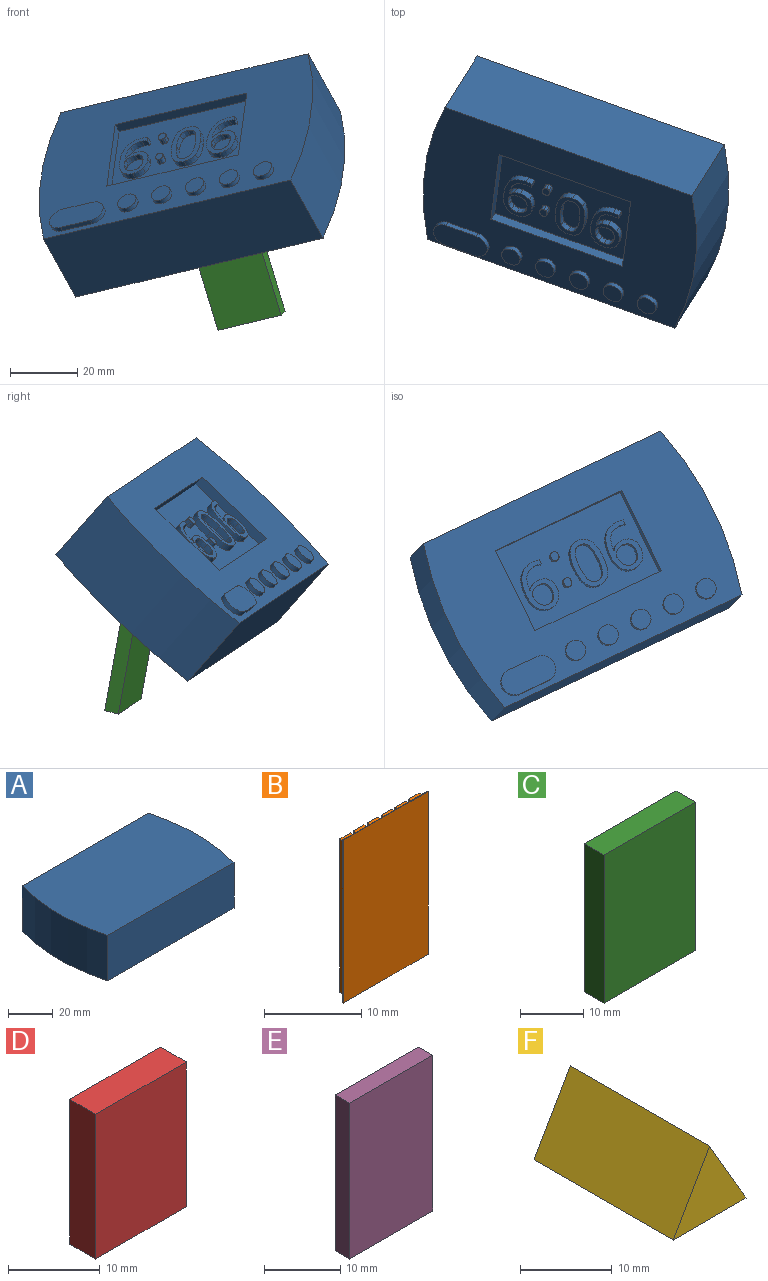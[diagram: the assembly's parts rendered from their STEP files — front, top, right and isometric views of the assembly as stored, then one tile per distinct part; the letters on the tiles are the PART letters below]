
ASSEMBLY  parts=6 mates=5
PART A: 116 faces, bbox 87.7x54.6x26.5 mm
  f0: plane 87.67x54.61mm, normal (0,0,-1), area 3248.2mm2, adj f1,f2,f3,f4,f6,f7,f8,f9
  f1: cylinder r=101.04mm len=54.61mm, axis (0,0,-1), area 1382.4mm2, adj f0,f2,f4,f5
  f2: plane 80.15x25mm, normal (0,-1,0), area 2003.7mm2, adj f0,f1,f3,f5
  f3: cylinder r=101.04mm len=54.61mm, axis (0,0,-1), area 1382.4mm2, adj f0,f2,f4,f5
  f4: plane 80.15x25mm, normal (0,1,0), area 2003.7mm2, adj f0,f1,f3,f5
  f5: plane 87.67x54.61mm, normal (0,0,1), area 4651.5mm2, adj f1,f2,f3,f4
  f6: plane 26.67x3mm, normal (1,0,0), area 80mm2, adj f0,f7,f9,f10
  f7: plane 42.67x3mm, normal (0,1,0), area 128mm2, adj f0,f6,f8,f10
  f8: plane 26.67x3mm, normal (-1,0,0), area 80mm2, adj f0,f7,f9,f10
  f9: plane 42.67x3mm, normal (0,-1,0), area 128mm2, adj f0,f6,f8,f10
  f10: plane 42.67x26.67mm, normal (0,0,-1), area 841.4mm2, adj f6,f7,f8,f9,f26,f27,f28,f29
  f11: cylinder r=3mm len=6mm, axis (0,0,1), area 28.3mm2, adj f0,f12
  f12: plane 6x6mm, normal (0,0,-1), area 28.3mm2, adj f11
  f13: cylinder r=3mm len=6mm, axis (0,0,1), area 28.3mm2, adj f0,f14
  f14: plane 6x6mm, normal (0,0,-1), area 28.3mm2, adj f13
  f15: cylinder r=3mm len=6mm, axis (0,0,1), area 28.3mm2, adj f0,f16
  f16: plane 6x6mm, normal (0,0,-1), area 28.3mm2, adj f15
  f17: cylinder r=3mm len=6mm, axis (0,0,1), area 28.3mm2, adj f0,f18
  f18: plane 6x6mm, normal (0,0,-1), area 28.3mm2, adj f17
  f19: cylinder r=3mm len=6mm, axis (0,0,1), area 28.3mm2, adj f0,f20
  f20: plane 6x6mm, normal (0,0,-1), area 28.3mm2, adj f19
  f21: plane 9.89x1.5mm, normal (-0.01,1,0), area 14.8mm2, adj f0,f22,f24,f25
  f22: cylinder r=3.92mm len=7.85mm, axis (0,0,1), area 18.5mm2, adj f0,f21,f23,f25
  f23: plane 9.46x1.5mm, normal (0,-1,0), area 14.2mm2, adj f0,f22,f24,f25
  f24: cylinder r=3.99mm len=7.95mm, axis (0,0,1), area 18.1mm2, adj f0,f21,f23,f25
  f25: plane 17.37x7.95mm, normal (0,0,-1), area 123.9mm2, adj f21,f22,f23,f24
  f26: extruded ~3.39x2mm, area 6.9mm2, adj f10,f27,f51,f52
  f27: extruded ~2.18x2mm, area 5.6mm2, adj f10,f26,f28,f52
  f28: extruded ~2.56x2mm, area 5.4mm2, adj f10,f27,f29,f52
  f29: extruded ~3.29x2mm, area 7.3mm2, adj f10,f28,f30,f52
  f30: extruded ~3.53x2mm, area 7.7mm2, adj f10,f29,f31,f52
  f31: extruded ~3.18x2mm, area 6.9mm2, adj f10,f30,f32,f52
  f32: extruded ~3.02x2mm, area 6.6mm2, adj f10,f31,f33,f52
  f33: extruded ~2.01x2mm, area 4.1mm2, adj f10,f32,f34,f52
  f34: extruded ~2x1.43mm, area 3.8mm2, adj f10,f33,f35,f52
  f35: plane 2x0.12mm, normal (0,1,0), area 0.2mm2, adj f10,f34,f36,f52
  f36: extruded ~4.46x2mm, area 9.5mm2, adj f10,f35,f37,f52
  f37: extruded ~3.55x2mm, area 8mm2, adj f10,f36,f38,f52
  f38: extruded ~2x1.78mm, area 3.6mm2, adj f10,f37,f39,f52
  f39: plane 2x1.4mm, normal (-1,0,0), area 2.8mm2, adj f10,f38,f40,f52
  f40: extruded ~2x1.8mm, area 3.6mm2, adj f10,f39,f51,f52
  f41: extruded ~2x1.65mm, area 3.5mm2, adj f42,f50,f52,f53
  f42: extruded ~2x1.37mm, area 3.6mm2, adj f41,f43,f52,f53
  f43: extruded ~2x1.9mm, area 3.9mm2, adj f42,f44,f52,f53
  f44: extruded ~2x1.31mm, area 2.8mm2, adj f43,f45,f52,f53
  f45: extruded ~2x1.18mm, area 3.1mm2, adj f44,f46,f52,f53
  f46: extruded ~2x1.64mm, area 3.4mm2, adj f45,f47,f52,f53
  f47: extruded ~2.15x2mm, area 4.7mm2, adj f46,f48,f52,f53
  f48: extruded ~2.22x2mm, area 4.8mm2, adj f47,f49,f52,f53
  f49: extruded ~2.51x2mm, area 5.4mm2, adj f48,f50,f52,f53
  f50: extruded ~2.17x2mm, area 4.9mm2, adj f41,f49,f52,f53
  f51: extruded ~8.41x6.51mm, area 24.3mm2, adj f10,f26,f40,f52
  f52: plane 14.73x9.36mm, normal (0,0,-1), area 53.2mm2, adj f26,f27,f28,f29,f30,f31,f32,f33
  f53: plane 6.44x6.11mm, normal (0,0,-1), area 31.7mm2, adj f41,f42,f43,f44,f45,f46,f47,f48
  f54: extruded ~5.48x2mm, area 11.4mm2, adj f10,f55,f69,f70
  f55: extruded ~3.54x2mm, area 8.4mm2, adj f10,f54,f56,f70
  f56: extruded ~3.56x2mm, area 8.4mm2, adj f10,f55,f57,f70
  f57: extruded ~5.56x2mm, area 11.5mm2, adj f10,f56,f58,f70
  f58: extruded ~5.51x2mm, area 11.4mm2, adj f10,f57,f59,f70
  f59: extruded ~3.52x2mm, area 8.4mm2, adj f10,f58,f60,f70
  f60: extruded ~3.58x2mm, area 8.4mm2, adj f10,f59,f69,f70
  f61: extruded ~4.54x2mm, area 9.3mm2, adj f62,f68,f70,f71
  f62: extruded ~2.34x2mm, area 5.8mm2, adj f61,f63,f70,f71
  f63: extruded ~2.36x2mm, area 5.9mm2, adj f62,f64,f70,f71
  f64: extruded ~4.52x2mm, area 9.2mm2, adj f63,f65,f70,f71
  f65: extruded ~4.54x2mm, area 9.3mm2, adj f64,f66,f70,f71
  f66: extruded ~2.36x2mm, area 5.9mm2, adj f65,f67,f70,f71
  f67: extruded ~2.34x2mm, area 5.8mm2, adj f66,f68,f70,f71
  f68: extruded ~4.55x2mm, area 9.3mm2, adj f61,f67,f70,f71
  f69: extruded ~5.55x2mm, area 11.5mm2, adj f10,f54,f60,f70
  f70: plane 14.76x9.48mm, normal (0,0,-1), area 54.2mm2, adj f54,f55,f56,f57,f58,f59,f60,f61
  f71: plane 11.94x6.16mm, normal (0,0,-1), area 62.2mm2, adj f61,f62,f63,f64,f65,f66,f67,f68
  f72: extruded ~2x1.01mm, area 2.2mm2, adj f10,f73,f79,f80
  f73: extruded ~2x0.83mm, area 1.8mm2, adj f10,f72,f74,f80
  f74: extruded ~2x0.88mm, area 1.9mm2, adj f10,f73,f75,f80
  f75: extruded ~2x0.98mm, area 2.1mm2, adj f10,f74,f76,f80
  f76: extruded ~2x1mm, area 2.1mm2, adj f10,f75,f77,f80
  f77: extruded ~2x0.89mm, area 2mm2, adj f10,f76,f78,f80
  f78: extruded ~2x0.86mm, area 1.9mm2, adj f10,f77,f79,f80
  f79: extruded ~2x1mm, area 2.1mm2, adj f10,f72,f78,f80
  f80: plane 2.66x2.36mm, normal (0,0,-1), area 5.2mm2, adj f72,f73,f74,f75,f76,f77,f78,f79
  f81: extruded ~2x1.01mm, area 2.2mm2, adj f10,f82,f86,f87
  f82: extruded ~2x0.83mm, area 1.8mm2, adj f10,f81,f83,f87
  f83: extruded ~2x0.88mm, area 1.9mm2, adj f10,f82,f84,f87
  f84: extruded ~2x0.98mm, area 2.1mm2, adj f10,f83,f85,f87
  f85: extruded ~2x1.32mm, area 4.1mm2, adj f10,f84,f86,f87
  f86: extruded ~2x1.32mm, area 4mm2, adj f10,f81,f85,f87
  f87: plane 2.65x2.36mm, normal (0,0,-1), area 5.2mm2, adj f81,f82,f83,f84,f85,f86
  f88: extruded ~3.39x2mm, area 6.9mm2, adj f10,f89,f113,f114
  f89: extruded ~2.18x2mm, area 5.6mm2, adj f10,f88,f90,f114
  f90: extruded ~2.56x2mm, area 5.4mm2, adj f10,f89,f91,f114
  f91: extruded ~3.29x2mm, area 7.3mm2, adj f10,f90,f92,f114
  f92: extruded ~3.53x2mm, area 7.7mm2, adj f10,f91,f93,f114
  f93: extruded ~3.18x2mm, area 6.9mm2, adj f10,f92,f94,f114
  f94: extruded ~3.02x2mm, area 6.6mm2, adj f10,f93,f95,f114
  f95: extruded ~2.01x2mm, area 4.1mm2, adj f10,f94,f96,f114
  f96: extruded ~2x1.43mm, area 3.8mm2, adj f10,f95,f97,f114
  f97: plane 2x0.12mm, normal (0,1,0), area 0.2mm2, adj f10,f96,f98,f114
  f98: extruded ~4.46x2mm, area 9.5mm2, adj f10,f97,f99,f114
  f99: extruded ~3.55x2mm, area 8mm2, adj f10,f98,f100,f114
  f100: extruded ~2x1.78mm, area 3.6mm2, adj f10,f99,f101,f114
  f101: plane 2x1.4mm, normal (-1,0,0), area 2.8mm2, adj f10,f100,f102,f114
  f102: extruded ~2x1.8mm, area 3.6mm2, adj f10,f101,f113,f114
  f103: extruded ~2x1.65mm, area 3.5mm2, adj f104,f112,f114,f115
  f104: extruded ~2x1.37mm, area 3.6mm2, adj f103,f105,f114,f115
  f105: extruded ~2x1.9mm, area 3.9mm2, adj f104,f106,f114,f115
  f106: extruded ~2x1.31mm, area 2.8mm2, adj f105,f107,f114,f115
  f107: extruded ~2x1.18mm, area 3.1mm2, adj f106,f108,f114,f115
  f108: extruded ~2x1.64mm, area 3.4mm2, adj f107,f109,f114,f115
  f109: extruded ~2.15x2mm, area 4.7mm2, adj f108,f110,f114,f115
  f110: extruded ~2.22x2mm, area 4.8mm2, adj f109,f111,f114,f115
  f111: extruded ~2.51x2mm, area 5.4mm2, adj f110,f112,f114,f115
  f112: extruded ~2.17x2mm, area 4.9mm2, adj f103,f111,f114,f115
  f113: extruded ~8.41x6.51mm, area 24.3mm2, adj f10,f88,f102,f114
  f114: plane 14.73x9.36mm, normal (0,0,-1), area 53.2mm2, adj f88,f89,f90,f91,f92,f93,f94,f95
  f115: plane 6.44x6.11mm, normal (0,0,-1), area 31.7mm2, adj f103,f104,f105,f106,f107,f108,f109,f110
PART B: 36 faces, bbox 12.3x1x20.5 mm
  f0: plane 19.27x0.9mm, normal (-1,0,0), area 17.3mm2, adj f1,f3,f4,f5
  f1: plane 1.5x0.9mm, normal (0,0,-1), area 1.3mm2, adj f0,f2,f4,f5
  f2: plane 19.27x0.9mm, normal (1,0,0), area 17.3mm2, adj f1,f3,f4,f5
  f3: plane 1.5x0.9mm, normal (0,0,1), area 1.3mm2, adj f0,f2,f4,f5
  f4: plane 19.27x1.5mm, normal (0,1,0), area 28.9mm2, adj f0,f1,f2,f3
  f5: plane 20.49x12.27mm, normal (0,1,0), area 77.9mm2, adj f0,f1,f2,f3,f6,f7,f8,f9
  f6: plane 19.27x0.9mm, normal (-1,0,0), area 17.3mm2, adj f5,f7,f9,f10
  f7: plane 1.5x0.9mm, normal (0,0,-1), area 1.4mm2, adj f5,f6,f8,f10
  f8: plane 19.27x0.9mm, normal (1,0,0), area 17.3mm2, adj f5,f7,f9,f10
  f9: plane 1.5x0.9mm, normal (0,0,1), area 1.4mm2, adj f5,f6,f8,f10
  f10: plane 19.27x1.5mm, normal (0,1,0), area 28.9mm2, adj f6,f7,f8,f9
  f11: plane 19.27x0.9mm, normal (-1,0,0), area 17.3mm2, adj f5,f12,f14,f15
  f12: plane 1.5x0.9mm, normal (0,0,-1), area 1.4mm2, adj f5,f11,f13,f15
  f13: plane 19.27x0.9mm, normal (1,0,0), area 17.3mm2, adj f5,f12,f14,f15
  f14: plane 1.5x0.9mm, normal (0,0,1), area 1.4mm2, adj f5,f11,f13,f15
  f15: plane 19.27x1.5mm, normal (0,1,0), area 28.9mm2, adj f11,f12,f13,f14
  f16: plane 19.27x0.9mm, normal (-1,0,0), area 17.3mm2, adj f5,f17,f19,f20
  f17: plane 1.5x0.9mm, normal (0,0,-1), area 1.4mm2, adj f5,f16,f18,f20
  f18: plane 19.27x0.9mm, normal (1,0,0), area 17.3mm2, adj f5,f17,f19,f20
  f19: plane 1.5x0.9mm, normal (0,0,1), area 1.4mm2, adj f5,f16,f18,f20
  f20: plane 19.27x1.5mm, normal (0,1,0), area 28.9mm2, adj f16,f17,f18,f19
  f21: plane 19.27x0.9mm, normal (-1,0,0), area 17.3mm2, adj f5,f22,f24,f25
  f22: plane 1.5x0.9mm, normal (0,0,-1), area 1.3mm2, adj f5,f21,f23,f25
  f23: plane 19.27x0.9mm, normal (1,0,0), area 17.3mm2, adj f5,f22,f24,f25
  f24: plane 1.5x0.9mm, normal (0,0,1), area 1.3mm2, adj f5,f21,f23,f25
  f25: plane 19.27x1.5mm, normal (0,1,0), area 28.9mm2, adj f21,f22,f23,f24
  f26: plane 19.27x0.9mm, normal (-1,0,0), area 17.3mm2, adj f5,f27,f29,f30
  f27: plane 1.5x0.9mm, normal (0,0,-1), area 1.4mm2, adj f5,f26,f28,f30
  f28: plane 19.27x0.9mm, normal (1,0,0), area 17.3mm2, adj f5,f27,f29,f30
  f29: plane 1.5x0.9mm, normal (0,0,1), area 1.4mm2, adj f5,f26,f28,f30
  f30: plane 19.27x1.5mm, normal (0,1,0), area 28.9mm2, adj f26,f27,f28,f29
  f31: plane 20.49x0.1mm, normal (-1,0,0), area 2mm2, adj f5,f32,f34,f35
  f32: plane 12.27x0.1mm, normal (0,0,-1), area 1.2mm2, adj f5,f31,f33,f35
  f33: plane 20.49x0.1mm, normal (1,0,0), area 2mm2, adj f5,f32,f34,f35
  f34: plane 12.27x0.1mm, normal (0,0,1), area 1.2mm2, adj f5,f31,f33,f35
  f35: plane 20.49x12.27mm, normal (0,-1,0), area 251.3mm2, adj f31,f32,f33,f34
PART C: 11 faces, bbox 20.5x4.3x28.8 mm
  f0: plane 28.78x20.49mm, normal (0,1,0), area 214.9mm2, adj f1,f2,f3,f4,f6,f7,f8,f9
  f1: plane 28.78x4.34mm, normal (-1,0,0), area 124.9mm2, adj f0,f2,f4,f5
  f2: plane 20.49x4.34mm, normal (0,0,-1), area 88.9mm2, adj f0,f1,f3,f5
  f3: plane 28.78x4.34mm, normal (1,0,0), area 124.9mm2, adj f0,f2,f4,f5
  f4: plane 20.49x4.34mm, normal (0,0,1), area 88.9mm2, adj f0,f1,f3,f5
  f5: plane 28.78x20.49mm, normal (0,-1,0), area 589.6mm2, adj f1,f2,f3,f4
  f6: plane 24.68x2mm, normal (1,0,0), area 49.4mm2, adj f0,f7,f9,f10
  f7: plane 15.19x2mm, normal (0,0,1), area 30.4mm2, adj f0,f6,f8,f10
  f8: plane 24.68x2mm, normal (-1,0,0), area 49.4mm2, adj f0,f7,f9,f10
  f9: plane 15.19x2mm, normal (0,0,-1), area 30.4mm2, adj f0,f6,f8,f10
  f10: plane 24.68x15.19mm, normal (0,1,0), area 374.8mm2, adj f6,f7,f8,f9
PART D: 6 faces, bbox 14x4x19.3 mm
  f0: plane 19.34x4mm, normal (-1,0,0), area 77.3mm2, adj f1,f3,f4,f5
  f1: plane 14x4mm, normal (0,0,-1), area 56mm2, adj f0,f2,f4,f5
  f2: plane 19.34x4mm, normal (1,0,0), area 77.3mm2, adj f1,f3,f4,f5
  f3: plane 14x4mm, normal (0,0,1), area 56mm2, adj f0,f2,f4,f5
  f4: plane 19.34x14mm, normal (0,1,0), area 270.7mm2, adj f0,f1,f2,f3
  f5: plane 19.34x14mm, normal (0,-1,0), area 270.7mm2, adj f0,f1,f2,f3
PART E: 6 faces, bbox 15.4x2.6x25 mm
  f0: plane 24.98x2.64mm, normal (-1,0,0), area 65.9mm2, adj f1,f3,f4,f5
  f1: plane 15.39x2.64mm, normal (0,0,-1), area 40.6mm2, adj f0,f2,f4,f5
  f2: plane 24.98x2.64mm, normal (1,0,0), area 65.9mm2, adj f1,f3,f4,f5
  f3: plane 15.39x2.64mm, normal (0,0,1), area 40.6mm2, adj f0,f2,f4,f5
  f4: plane 24.98x15.39mm, normal (0,1,0), area 384.4mm2, adj f0,f1,f2,f3
  f5: plane 24.98x15.39mm, normal (0,-1,0), area 384.4mm2, adj f0,f1,f2,f3
PART F: 5 faces, bbox 11.3x21.5x9.8 mm
  f0: plane 21.47x9.76mm, normal (0.87,0,0.5), area 242mm2, adj f1,f2,f3,f4
  f1: plane 21.47x9.76mm, normal (-0.87,0,0.5), area 242mm2, adj f0,f2,f3,f4
  f2: plane 21.47x11.27mm, normal (0,0,-1), area 242mm2, adj f0,f1,f3,f4
  f3: plane 11.27x9.76mm, normal (0,1,0), area 55mm2, adj f0,f1,f2
  f4: plane 11.27x9.76mm, normal (0,-1,0), area 55mm2, adj f0,f1,f2
PLACE A rot(axis=(0.12,0.92,0.36),160.9deg) t=(177.26,-27.3,7.87)mm
PLACE B rot(axis=(-0.04,-0.97,-0.23),106.8deg) t=(194.59,-19.37,44.81)mm
PLACE C rot(axis=(0.16,0.98,0.11),165.1deg) t=(147.28,10.63,-13.88)mm
PLACE D rot(axis=(-0.04,-0.97,-0.23),106.8deg) t=(191.54,-22.11,42.37)mm
PLACE E rot(axis=(-0.13,-0.11,0.99),162.1deg) t=(163.36,20.5,-65.45)mm
PLACE F rot(axis=(-0.28,0.08,0.96),71deg) t=(218.43,7.53,-63.12)mm
MATE fastened B.f35 <-> D.f4  axis (-0.27,-0.93,-0.25) through (190.13,-3.29,-9.84)mm
MATE fastened D.f5 <-> F.f0  axis (-0.27,-0.93,-0.25) through (189.03,-7,-10.84)mm
MATE fastened E.f4 <-> C.f10  axis (-0.27,-0.93,-0.25) through (195.93,-1.43,-30.38)mm
MATE fastened F.f1 <-> A.f5  axis (-0.38,-0.61,0.69) through (186.89,-12.01,-9.41)mm
MATE fastened C.f2 <-> D.f0  axis (-0.29,-0.17,0.94) through (191.58,-3.96,-16.94)mm
